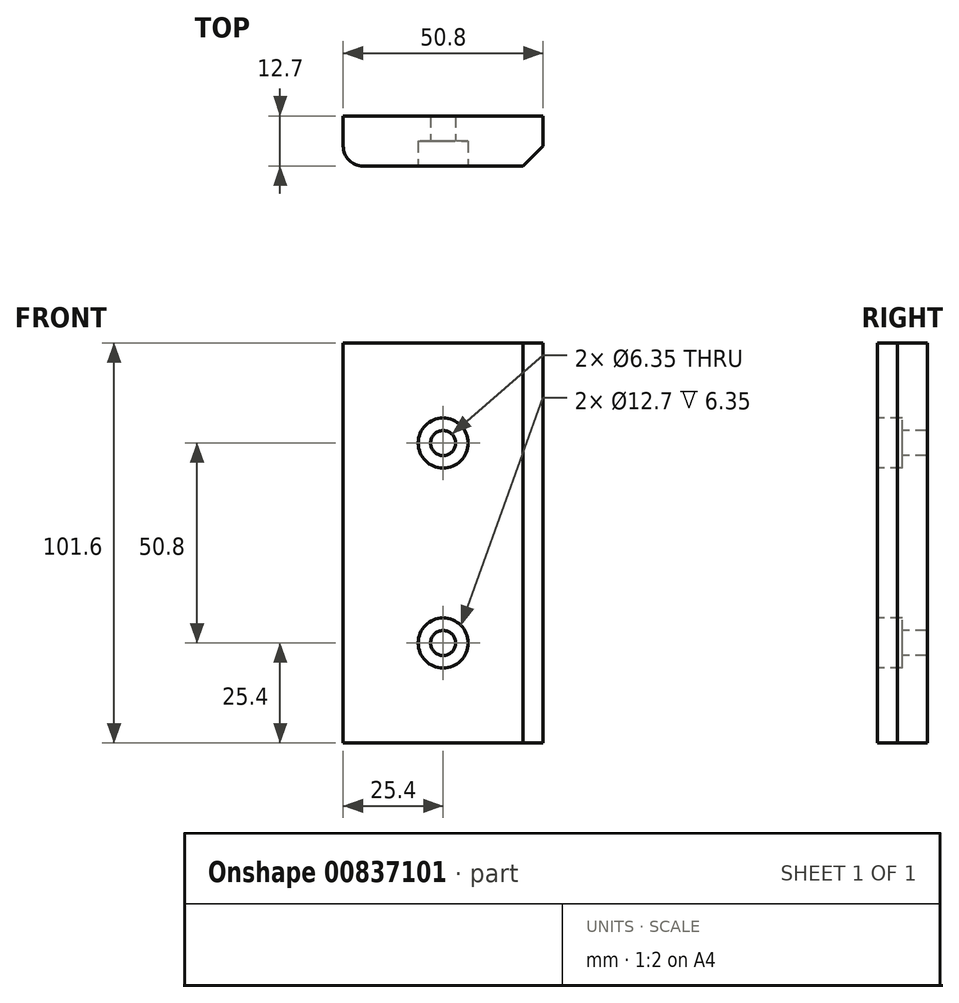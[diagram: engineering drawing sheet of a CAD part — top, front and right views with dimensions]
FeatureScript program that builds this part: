
annotation { "Feature Type Name" : "Feature", "Feature Type Description" : "" }
export const myFeature = defineFeature(function(context is Context, id is Id, definition is map)
    precondition{}
    {
        {
            var Q0;
            Q0=qCreatedBy(makeId("Front.planeOp"),FACE);
            var sketch = newSketch(context, id + "F0", { "sketchPlane" : qUnion([Q0])});
            skLineSegment(sketch, "E0.bottom", {"start": v(25.4, -50.8) * mm, "end": v(-25.4, -50.8) * mm});
            skLineSegment(sketch, "E0.top", {"start": v(25.4, 50.8) * mm, "end": v(-25.4, 50.8) * mm});
            skLineSegment(sketch, "E0.left", {"start": v(25.4, -50.8) * mm, "end": v(25.4, 50.8) * mm});
            skLineSegment(sketch, "E0.right", {"start": v(-25.4, -50.8) * mm, "end": v(-25.4, 50.8) * mm});
            skLineSegment(sketch, "E1", {"start": v(25.4, 0) * mm, "end": v(-25.4, 0) * mm, "construction": true});
            skLineSegment(sketch, "E2", {"start": v(0, 50.8) * mm, "end": v(0, -50.8) * mm, "construction": true});
            skSolve(sketch);
        }
        {
            var Q0;
            Q0=makeQuery(id+"F0.imprint","IMPRINT",FACE,{"disambiguationData":[TD([[makeQuery(id+"F0.imprint","IMPRINT",EDGE,{"derivedFrom":sQuery(id+"F0.wireOp",EDGE,"E0.bottom")}),-1.0]])]});
            extrude(context, id + "F1", {"entities" : qUnion([Q0]), "depth" : 12.7 * mm, "offsetDistance" : 25.4 * mm});
        }
        {
            var Q0;
            Q0=makeQuery(id+"F1.opExtrude","CAP_FACE",FACE,{"disambiguationData":[OSD([sQuery(id+"F0.wireOp",EDGE,"E0.bottom"),sQuery(id+"F0.wireOp",EDGE,"E0.top"),sQuery(id+"F0.wireOp",EDGE,"E0.left"),sQuery(id+"F0.wireOp",EDGE,"E0.right")])],"isStart":false});
            var sketch = newSketch(context, id + "F2", { "sketchPlane" : qUnion([Q0])});
            skPoint(sketch, "E3", {"position": v(0, 25.4) * mm});
            skPoint(sketch, "E4", {"position": v(0, -25.4) * mm});
            skLineSegment(sketch, "E5", {"start": v(-36.3, 0) * mm, "end": v(50.5, 0) * mm, "construction": true});
            skSolve(sketch);
        }
        {
            var Q0;
            Q0=sQuery(id+"F2.wireOp",VERTEX,"E3");
            var Q1;
            Q1=sQuery(id+"F2.wireOp",VERTEX,"E4");
            var Q2;
            Q2=makeQuery(id+"F1.opExtrude","SWEPT_BODY",BODY,{"disambiguationData":[OSD([sQuery(id+"F0.wireOp",EDGE,"E0.bottom"),sQuery(id+"F0.wireOp",EDGE,"E0.top"),sQuery(id+"F0.wireOp",EDGE,"E0.left"),sQuery(id+"F0.wireOp",EDGE,"E0.right")])]});
            hole(context, id + "F3", {"style" : HoleStyle.C_BORE, "endStyle" : HoleEndStyle.THROUGH, "holeDiameter" : 6.35 * mm, "cBoreDiameter" : 12.7 * mm, "cBoreDepth" : 6.35 * mm, "majorDiameter" : 6.35 * mm, "isTappedThrough" : true, "tappedDepth" : 12.7 * mm, "tapClearance" : 3, "locations" : qUnion([Q0, Q1]), "scope" : qUnion([Q2])});
        }
        {
            var Q0;
            Q0=makeQuery(id+"F1.opExtrude","CAP_EDGE",EDGE,{"disambiguationData":[OSD([sQuery(id+"F0.wireOp",EDGE,"E0.right")])],"isStart":false});
            fillet(context, id + "F4", {"entities" : qUnion([Q0]), "radius" : 5.08 * mm, "tangentPropagation" : true, "allowEdgeOverflow" : false});
        }
        {
            var Q0;
            Q0=makeQuery(id+"F1.opExtrude","CAP_EDGE",EDGE,{"disambiguationData":[OSD([sQuery(id+"F0.wireOp",EDGE,"E0.left")])],"isStart":false});
            chamfer(context, id + "F5", {"entities" : qUnion([Q0]), "width" : 5.08 * mm, "tangentPropagation" : true});
        }
    });
